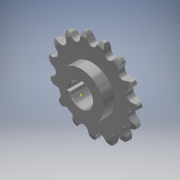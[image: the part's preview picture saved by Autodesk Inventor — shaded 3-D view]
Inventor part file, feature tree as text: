
AUTODESK INVENTOR PART (.ipt)
format: ipt  version: 2017.1 (Build 211199000, 199)  size: 504,320 bytes
history: native  units: mm
features: other x7, extrude x6, sketch x4, pattern_linear x1, pattern_circular x1, plane x1, chamfer x1
ambient origin geometry x8: Origin, YZ Plane, XZ Plane, XY Plane, X Axis, Y Axis, Z Axis, Center Point
bodies: Solid1 (feature_tree)
feature tree (21):
  other  "fc17-011_Sprocket"
  other  "Theoretical Tooth Profile"
  other  "Tooth Profile"
  other  "Section Profile"
  other  "Shroud"
  other  "Strand"
  pattern_linear  "Strand Pattern"  Spacing1=2.490003mm  [1 undecoded]
  extrude  "Theoretical Tooth"  Depth=6.3754mm
  extrude  "Tooth"  Depth=6.3754mm
  pattern_circular  "Tooth Pattern"  [2 undecoded]
  other  "Timing Plane"
  plane  "Work Plane3"
  extrude  "Extrusion4"  Depth=10.0mm TaperAngle=0.0deg
  sketch  "Sketch5"  dims[d2=4.18879mm]
  extrude  "Extrusion5"  Depth=6.3754mm
  extrude  "Extrusion6"  TaperAngle=360.0deg  [1 undecoded]
  sketch  "Sketch6"  dims[d3=2.5908mm]
  extrude  "Key Square (Hole)1"  Depth=6.3754mm
  chamfer  "Chamfer1"  [1 undecoded]
  sketch  "Sketch4"  dims[d0=45.81272mm]
  sketch  "Sketch8"  dims[d10=22.514747mm d11=2.490003mm d12=4.064mm d13=6.6548mm d14=7.112mm d18=10.0mm d19=0.0mm d20=150.0mm d21=360.0deg d23=2.8575mm d28=0.0mm d29=0.0mm d30=4.593336mm d31=33.762602mm d32=4.593336mm d33=1.190625mm d34=10.125075mm d36=90.0deg d37=90.0deg d38=10.0mm d40=10.1346mm d42=0.0mm d43=2.296668mm d44=23.387412mm d45=2.5908mm d46=10.3632mm d47=0.0mm d48=25.4mm d49=0.0mm d50=10.0mm d51=4.064mm d52=2.032mm d53=69.65mm d54=0.0mm d55=12.7508mm d56=25.4mm d57=6.223mm d58=0.0mm d59=25.777mm d60=0.0mm d66=6.3754mm d67=3.175mm d68=7.9629mm d69=7.9629mm d70=0.0mm d71=0.508mm d72=3.175mm d73=45.0deg]
note: 5 required parameter values undecoded (feature->parameter linkage not recoverable at this tier; creation-order binding heuristic only, values carry confidence <= 0.55)
